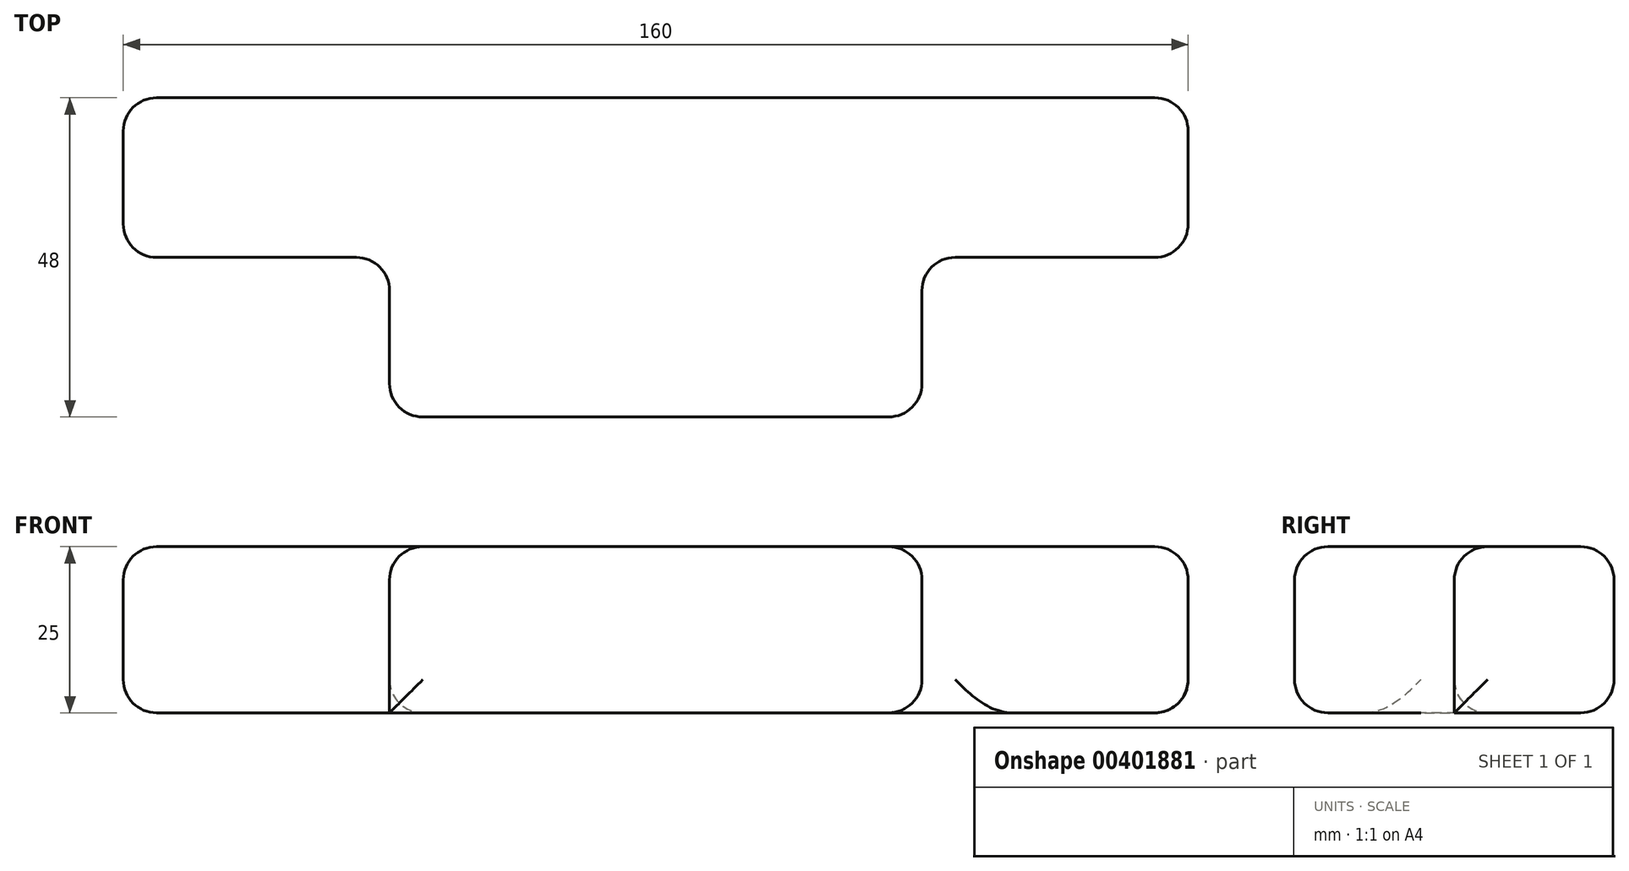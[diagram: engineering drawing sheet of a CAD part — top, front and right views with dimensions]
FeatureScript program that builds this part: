
annotation { "Feature Type Name" : "Feature", "Feature Type Description" : "" }
export const myFeature = defineFeature(function(context is Context, id is Id, definition is map)
    precondition{}
    {
        {
            var Q0;
            Q0=qCreatedBy(makeId("Top.planeOp"),FACE);
            var sketch = newSketch(context, id + "F0", { "sketchPlane" : qUnion([Q0])});
            skLineSegment(sketch, "E0.bottom", {"start": v(-80, 50.4) * mm, "end": v(0, 50.4) * mm});
            skLineSegment(sketch, "E0.top", {"start": v(-80, 26.4) * mm, "end": v(-40, 26.4) * mm});
            skLineSegment(sketch, "E0.left", {"start": v(-80, 50.4) * mm, "end": v(-80, 26.4) * mm});
            skLineSegment(sketch, "E1.bottom", {"start": v(0, 50.4) * mm, "end": v(80, 50.4) * mm});
            skLineSegment(sketch, "E1.top", {"start": v(40, 26.4) * mm, "end": v(80, 26.4) * mm});
            skLineSegment(sketch, "E1.right", {"start": v(80, 50.4) * mm, "end": v(80, 26.4) * mm});
            skLineSegment(sketch, "E2.top", {"start": v(-40, 2.4) * mm, "end": v(40, 2.4) * mm});
            skLineSegment(sketch, "E2.left", {"start": v(-40, 26.4) * mm, "end": v(-40, 2.4) * mm});
            skLineSegment(sketch, "E2.right", {"start": v(40, 26.4) * mm, "end": v(40, 2.4) * mm});
            skPoint(sketch, "E0.right.end.orphan", {"position": v(0, 26.4) * mm});
            skSolve(sketch);
        }
        {
            var Q0;
            Q0=makeQuery(id+"F0.imprint","IMPRINT",FACE,{"disambiguationData":[TD([[makeQuery(id+"F0.imprint","IMPRINT",EDGE,{"derivedFrom":sQuery(id+"F0.wireOp",EDGE,"E0.bottom")}),-1.0]])]});
            extrude(context, id + "F1", {"entities" : qUnion([Q0]), "depth" : 25 * mm});
        }
        {
            var Q0;
            Q0=makeQuery(id+"F1.opExtrude","CAP_EDGE",EDGE,{"disambiguationData":[OSD([sQuery(id+"F0.wireOp",EDGE,"E2.top")])],"isStart":false});
            var Q1;
            Q1=makeQuery(id+"F1.opExtrude","CAP_EDGE",EDGE,{"disambiguationData":[OSD([sQuery(id+"F0.wireOp",EDGE,"E2.left")])],"isStart":false});
            var Q2;
            Q2=makeQuery(id+"F1.opExtrude","CAP_FACE",FACE,{"disambiguationData":[OSD([sQuery(id+"F0.wireOp",EDGE,"E0.bottom"),sQuery(id+"F0.wireOp",EDGE,"E0.left"),sQuery(id+"F0.wireOp",EDGE,"E1.bottom"),sQuery(id+"F0.wireOp",EDGE,"E1.right"),sQuery(id+"F0.wireOp",EDGE,"E2.top"),sQuery(id+"F0.wireOp",EDGE,"E2.left"),sQuery(id+"F0.wireOp",EDGE,"E2.right"),sQuery(id+"F0.wireOp",EDGE,"E0.top"),sQuery(id+"F0.wireOp",EDGE,"E1.top")])],"isStart":false});
            var Q3;
            Q3=makeQuery(id+"F1.opExtrude","SWEPT_EDGE",EDGE,{"disambiguationData":[OSD([sQuery(id+"F0.wireOp",EDGE,"E2.top"),sQuery(id+"F0.wireOp",EDGE,"E2.right")])]});
            var Q4;
            Q4=makeQuery(id+"F1.opExtrude","CAP_EDGE",EDGE,{"disambiguationData":[OSD([sQuery(id+"F0.wireOp",EDGE,"E2.top")])],"isStart":true});
            var Q5;
            Q5=makeQuery(id+"F1.opExtrude","CAP_EDGE",EDGE,{"disambiguationData":[OSD([sQuery(id+"F0.wireOp",EDGE,"E2.right")])],"isStart":true});
            var Q6;
            Q6=makeQuery(id+"F1.opExtrude","SWEPT_EDGE",EDGE,{"disambiguationData":[OSD([sQuery(id+"F0.wireOp",EDGE,"E2.right"),sQuery(id+"F0.wireOp",EDGE,"E1.top")])]});
            var Q7;
            Q7=makeQuery(id+"F1.opExtrude","CAP_EDGE",EDGE,{"disambiguationData":[OSD([sQuery(id+"F0.wireOp",EDGE,"E1.top")])],"isStart":true});
            var Q8;
            Q8=makeQuery(id+"F1.opExtrude","SWEPT_EDGE",EDGE,{"disambiguationData":[OSD([sQuery(id+"F0.wireOp",EDGE,"E1.right"),sQuery(id+"F0.wireOp",EDGE,"E1.top")])]});
            var Q9;
            Q9=makeQuery(id+"F1.opExtrude","CAP_EDGE",EDGE,{"disambiguationData":[OSD([sQuery(id+"F0.wireOp",EDGE,"E1.right")])],"isStart":true});
            var Q10;
            Q10=makeQuery(id+"F1.opExtrude","SWEPT_EDGE",EDGE,{"disambiguationData":[OSD([sQuery(id+"F0.wireOp",EDGE,"E1.bottom"),sQuery(id+"F0.wireOp",EDGE,"E1.right")])]});
            var Q11;
            Q11=makeQuery(id+"F1.opExtrude","SWEPT_EDGE",EDGE,{"disambiguationData":[OSD([sQuery(id+"F0.wireOp",EDGE,"E2.top"),sQuery(id+"F0.wireOp",EDGE,"E2.left")])]});
            var Q12;
            Q12=makeQuery(id+"F1.opExtrude","SWEPT_FACE",FACE,{"disambiguationData":[OSD([sQuery(id+"F0.wireOp",EDGE,"E0.top")])]});
            var Q13;
            Q13=makeQuery(id+"F1.opExtrude","SWEPT_EDGE",EDGE,{"disambiguationData":[OSD([sQuery(id+"F0.wireOp",EDGE,"E0.bottom"),sQuery(id+"F0.wireOp",EDGE,"E0.left")])]});
            var Q14;
            Q14=makeQuery(id+"F1.opExtrude","CAP_EDGE",EDGE,{"disambiguationData":[OSD([sQuery(id+"F0.wireOp",EDGE,"E0.left")])],"isStart":true});
            var Q15;
            Q15=makeQuery(id+"F1.opExtrude","CAP_EDGE",EDGE,{"disambiguationData":[OSD([sQuery(id+"F0.wireOp",EDGE,"E0.bottom"),sQuery(id+"F0.wireOp",EDGE,"E1.bottom")])],"isStart":true});
            fillet(context, id + "F2", {"entities" : qUnion([Q0, Q1, Q2, Q3, Q4, Q5, Q6, Q7, Q8, Q9, Q10, Q11, Q12, Q13, Q14, Q15]), "radius" : 5 * mm, "tangentPropagation" : true, "allowEdgeOverflow" : false});
        }
    });
